# Revit family: Kessel 28767 en
name_source: partatom
category: Plumbing Fixtures
revit_build: Autodesk Revit Architecture 2014 (Build: 20130308_1515(x64)
units: mm (PartAtom-declared; Revit-internal decimal feet)

## types (1)
- Kessel 28767 en
    <1.010.00.2> Number of the part of the guideline = 4
    <1.010.00.3> Issue date (month) of the guideline = 201410
    <1.010.00.4> Manufacturer name = Kessel
    <1.010.00.5> Revision date of the file = 20190228
    <1.800.00.3> BS number = 00400400010000200200100100000200100100200000000026???
    <1.800.00.4> Comment field = Aqualift F Duo, Comfort, SPF 3000-S3, gate valve
    <1.810.00.3> Manufacturer’s reference number = 28767
    <1.810.00.4> DATANORM number = 28767
    <1.810.00.6> GTIN number = 4026092054581
    <1.960/3L.00.8> Link (URL) = http://www.kessel.de
    <4.100.00.4> Area of application = drainage
    <4.110.00.4> Model series = Lifting station Aqualift F
    <4.200.00.3> Design type = Freestanding pump
    <4.250.00.3> Shaft position = vertical
    <4.260.00.3> Construction = dry-rotor pump
    <4.300.00.3> Hydraulic = single-level
    <4.350.00.3> Intake feature = normal-priming
    <4.400.00.3> Actuator = e-motor for three-phase current
    <4.450.00.3> Type of speed adjustment = none
    <4.460.00.3> E-motor startup mode = direct
    <4.500.00.3> Material specifications pump housing = Cast iron
    <4.700.00.10> Star / delta starting circuit with three-phase connection or three-phase current = yes
    <4.700.00.11> Rated frequency [Hz] = 50
    <4.700.00.12> Degree of protection = IP 68
    <4.700.00.13> Heat class = F
    <4.700.00.15> Maximum temperature of pumped medium [°C] = 40
    <4.700.00.16> Minimum temperature of pumped medium [°C] = 0
    <4.700.00.21> Maximum working pressure Pmax PN [hPa] = 1600
    <4.700.00.22> Maximum shaft output (P2) per pump/drive [W] = 2.7
    <4.700.00.23> Nominal speed n [1/min] = 2845
    <4.700.00.24> Maximum speed n [1/min] = 2845
    <4.700.00.25> minimum speed at int. speed adjustment [1/min] = 0
    <4.700.00.26> maximum power consumption per pump / drive [A] = 5.4
    <4.700.00.27> inrush current [A] = 41
    <4.700.00.28> Motor-pump shaft = continuous
    <4.700.00.29> shaft seal = Mechanical seal
    <4.700.00.30> Total number of pumps / drives = 2
    <4.700.00.31> Number of operating pumps / drives = 1
    <4.700.00.32> Net mass [kg] = 91.55
    <4.700.00.33> electrical rating (P1) [W] = 3.2
    <4.700.00.34> maximum flow [m3/h] = 47
    <4.700.00.37> maximum delivery height [m] = 16
    <4.700.00.44> upper tolerance of the operating voltage (+) [%] = 10
    <4.700.00.45> lower tolerance of the operating voltage (-) [%] = 10
    <4.700.00.46> vertical installation = yes
    <4.700.00.47> outdoor installation = no
    <4.700.00.48> ATEX = no
    <4.700.00.49> protection class = protection class I
    <4.700.00.4> Product name = Aqualift F Duo, Comfort, SPF 3000-S3, gate valve
    <4.700.00.50> motor protection = internal
    <4.700.00.6> Nominal connection size on pressure side = 100
    <4.700.00.7> Nominal connection size on suction side = 100
    <4.700.00.8> Electrical connection [V] = 400
    <4.700.00.9> Voltage = 3/N/PE 400V
    <4.710.01.10> Type of wastewater disposal plant = Double unit (duo)
    <4.710.01.11> Installation site of the plant = Overground (free-standing)
    <4.710.01.13> Mass pump (net) [kg] = 24
    <4.710.01.14> Mass overall system (net) [kg] = 91.55
    <4.710.01.18> Backflow preventer available = yes
    <4.710.01.19> Type of level control = Immersion tube, with air bubbling
    <4.710.01.20> ATEX for switching device = no
    <4.710.01.21> Function switching device = with alarm message
    <4.710.01.22> Variant of the warning device = acoustic signal tone
    <4.710.01.23> Self-diagnosis system for switching device (SDS) = yes
    <4.710.01.24> Logbook function for warning device = yes
    <4.710.01.25> Interface for switching device available = Radio interface (GSM)
    <4.710.01.26> Connection for switching device to GLT, GA = optional
    <4.710.01.27> Display for switching device = yes
    <4.710.01.28> Battery operation of the warning device possible = yes
    <4.710.01.3> Volume collection container [l] = 120
    <4.710.01.4> Deliverable volume between on and off volume of the collection container [l] = 50
    <4.710.01.5> Cutting device available = no
    <4.710.01.6> free ball passage [mm] = 40
    <4.710.01.7> operating mode = S3
    <4.710.01.8> Type of S2 / S3 operation = 50%
    <4.710.01.9> Type of wastewater plant = Sewage lifting unit (EN 12050-1)
    <4.710.02.10> Mass pump (net) [kg] = 24
    <4.710.02.3> free ball passage [mm] = 40
    <4.710.02.4> Attached pump control = yes
    <4.710.02.5> cutter = no
    <4.710.02.6> operating mode = S3
    <4.710.02.7> Type of S2 / S3 operation = 50%
    <4.710.02.8> Application of the wastewater pump = Sewage lifting unit (EN 12050-1)
    <4.710.02.9> Location of the pump = Overground (free-standing)
    <4.710.03.3> Type of measurements = Dimensions
    <4.710.03.4> length [mm] = 773
    <4.710.03.5> width [mm] = 780
    <4.710.03.6> height [mm] = 788
    <4.710.03.7> Mass (net) [kg] = 91.55
    CONNECTOR0_DIAMETER_dY_0r = 0 mm  [stored 0 ft]
    CONNECTOR0_dY_00 = 90 mm
    CONNECTOR0_dY_01 = 165 mm  [stored 0.541339 ft]
    CONNECTOR0_ref_dX = 230 mm
    CONNECTOR0_ref_dY = 90 mm
    CONNECTOR0_ref_dZ = 301 mm
    CONNECTOR10_DIAMETER_dX_0r = 0 mm  [stored 0 ft]
    CONNECTOR10_dX_00 = 381 mm  [stored 1.25 ft]
    CONNECTOR10_dX_01 = 391 mm
    CONNECTOR10_ref_dX = 381 mm  [stored 1.25 ft]
    CONNECTOR10_ref_dY = 75 mm
    CONNECTOR10_ref_dZ = 214 mm  [stored 0.7021 ft]
    CONNECTOR11_DIAMETER_dY_0r = 0 mm  [stored 0 ft]
    CONNECTOR11_dY_00 = 90 mm
    CONNECTOR11_dY_01 = 165 mm  [stored 0.541339 ft]
    CONNECTOR11_ref_dX = 230 mm
    CONNECTOR11_ref_dY = 90 mm
    CONNECTOR11_ref_dZ = 81 mm
    CONNECTOR1_DIAMETER_dZ_0r = 0 mm  [stored 0 ft]
    CONNECTOR1_dZ_00 = 388 mm
    CONNECTOR1_dZ_01 = 471 mm
    CONNECTOR1_ref_dZ = 388 mm
    CONNECTOR2_DIAMETER_dZ_0r = 0 mm  [stored 0 ft]
    CONNECTOR2_dZ_00 = 447 mm
    CONNECTOR2_dZ_01 = 457 mm
    CONNECTOR2_ref_dX = 185 mm
    CONNECTOR2_ref_dY = 365 mm
    CONNECTOR2_ref_dZ = 447 mm
    CONNECTOR3_DIAMETER_dZ_0r = 0 mm  [stored 0 ft]
    CONNECTOR3_dZ_00 = 447 mm
    CONNECTOR3_dZ_01 = 457 mm
    CONNECTOR3_ref_dX = 185 mm
    CONNECTOR3_ref_dY = 365 mm
    CONNECTOR3_ref_dZ = 447 mm
    CONNECTOR4_DIAMETER_dZ_0r = 0 mm  [stored 0 ft]
    CONNECTOR4_dZ_00 = 427 mm
    CONNECTOR4_dZ_01 = 437 mm
    CONNECTOR4_ref_dX = 231 mm
    CONNECTOR4_ref_dY = 75 mm
    CONNECTOR4_ref_dZ = 427 mm
    CONNECTOR5_DIAMETER_dY_0r = 0 mm  [stored 0 ft]
    CONNECTOR5_dY_00 = 86 mm  [stored 0.282152 ft]
    CONNECTOR5_dY_01 = 96 mm
    CONNECTOR5_ref_dX = 1 mm  [stored 0.00328084 ft]
    CONNECTOR5_ref_dY = 86 mm  [stored 0.282152 ft]
    CONNECTOR5_ref_dZ = 214 mm  [stored 0.7021 ft]
    CONNECTOR6_DIAMETER_dY_0r = 0 mm  [stored 0 ft]
    CONNECTOR6_dY_00 = 81 mm
    CONNECTOR6_dY_01 = 91 mm
    CONNECTOR6_ref_dX = 230 mm
    CONNECTOR6_ref_dY = 81 mm
    CONNECTOR6_ref_dZ = 214 mm  [stored 0.7021 ft]
    CONNECTOR7_DIAMETER_dY_0r = 0 mm  [stored 0 ft]
    CONNECTOR7_dY_00 = 686 mm
    CONNECTOR7_dY_01 = 626 mm
    CONNECTOR7_ref_dY = 626 mm
    CONNECTOR7_ref_dZ = 591 mm
    CONNECTOR8_DIAMETER_dZ_0r = 0 mm  [stored 0 ft]
    CONNECTOR8_dZ_00 = 388 mm
    CONNECTOR8_dZ_01 = 461 mm
    CONNECTOR8_ref_dY = 115 mm
    CONNECTOR8_ref_dZ = 388 mm
    CONNECTOR9_DIAMETER_dX_0r = 0 mm  [stored 0 ft]
    CONNECTOR9_dX_00 = 391 mm
    CONNECTOR9_dX_01 = 381 mm  [stored 1.25 ft]
    CONNECTOR9_ref_dX = 381 mm  [stored 1.25 ft]
    CONNECTOR9_ref_dY = 75 mm
    CONNECTOR9_ref_dZ = 214 mm  [stored 0.7021 ft]
    Manufacturer = Kessel
    Model = 28767
    URL = www.kessel.com

note: [stored X ft] marks values corroborated as IEEE doubles in the binary element streams (Revit-internal decimal feet)
